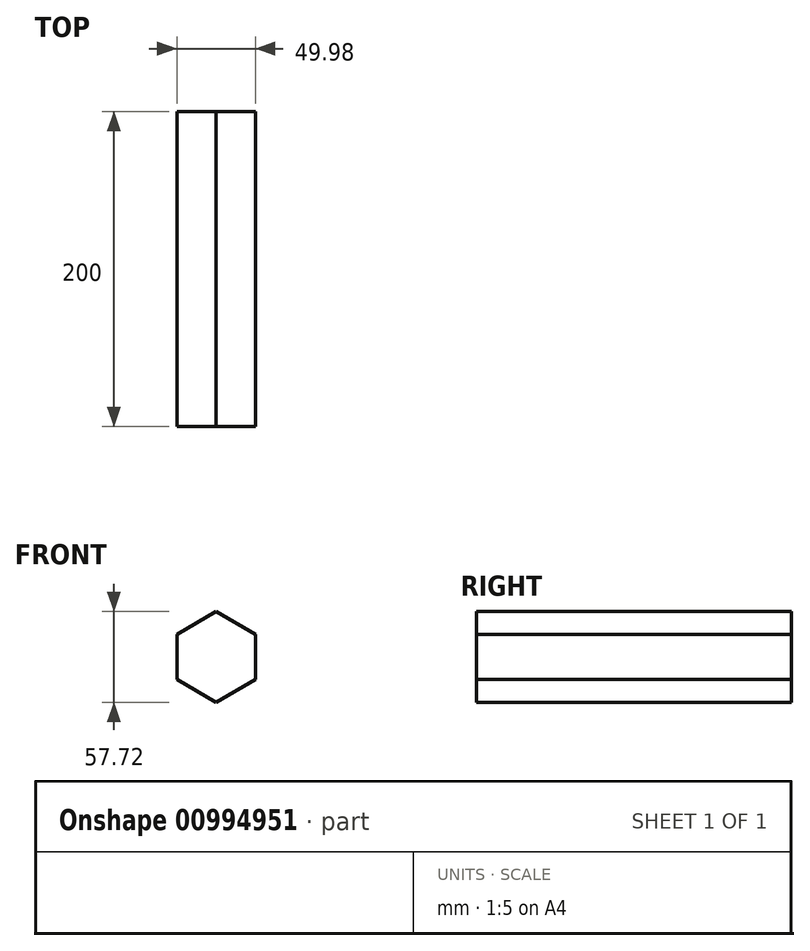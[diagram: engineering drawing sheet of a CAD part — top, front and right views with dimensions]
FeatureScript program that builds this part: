
annotation { "Feature Type Name" : "Feature", "Feature Type Description" : "" }
export const myFeature = defineFeature(function(context is Context, id is Id, definition is map)
    precondition{}
    {
        {
            var Q0;
            Q0=qCreatedBy(makeId("Front.planeOp"),FACE);
            var sketch = newSketch(context, id + "F0", { "sketchPlane" : qUnion([Q0])});
            skCircle(sketch, "E0.cCircle", {"center": v(0, 0) * mm, "radius": 25 * mm, "construction": true});
            skLineSegment(sketch, "E0.0", {"start": v(25, 14.43) * mm, "end": v(25, -14.43) * mm});
            skLineSegment(sketch, "E0.1", {"start": v(25, -14.43) * mm, "end": v(0, -28.86) * mm});
            skLineSegment(sketch, "E0.2", {"start": v(0, -28.86) * mm, "end": v(-25, -14.43) * mm});
            skLineSegment(sketch, "E0.3", {"start": v(-25, -14.43) * mm, "end": v(-25, 14.43) * mm});
            skLineSegment(sketch, "E0.4", {"start": v(-25, 14.43) * mm, "end": v(0, 28.86) * mm});
            skLineSegment(sketch, "E0.5", {"start": v(0, 28.86) * mm, "end": v(25, 14.43) * mm});
            skPoint(sketch, "E0.0.midPoint", {"position": v(25, 0) * mm});
            skSolve(sketch);
        }
        {
            var Q0;
            Q0 = qSketchRegion(id + "F0", true);
            extrude(context, id + "F1", {"entities" : qUnion([Q0]), "endBound" : BoundingType.SYMMETRIC, "depth" : 200 * mm, "offsetDistance" : 25 * mm});
        }
    });
